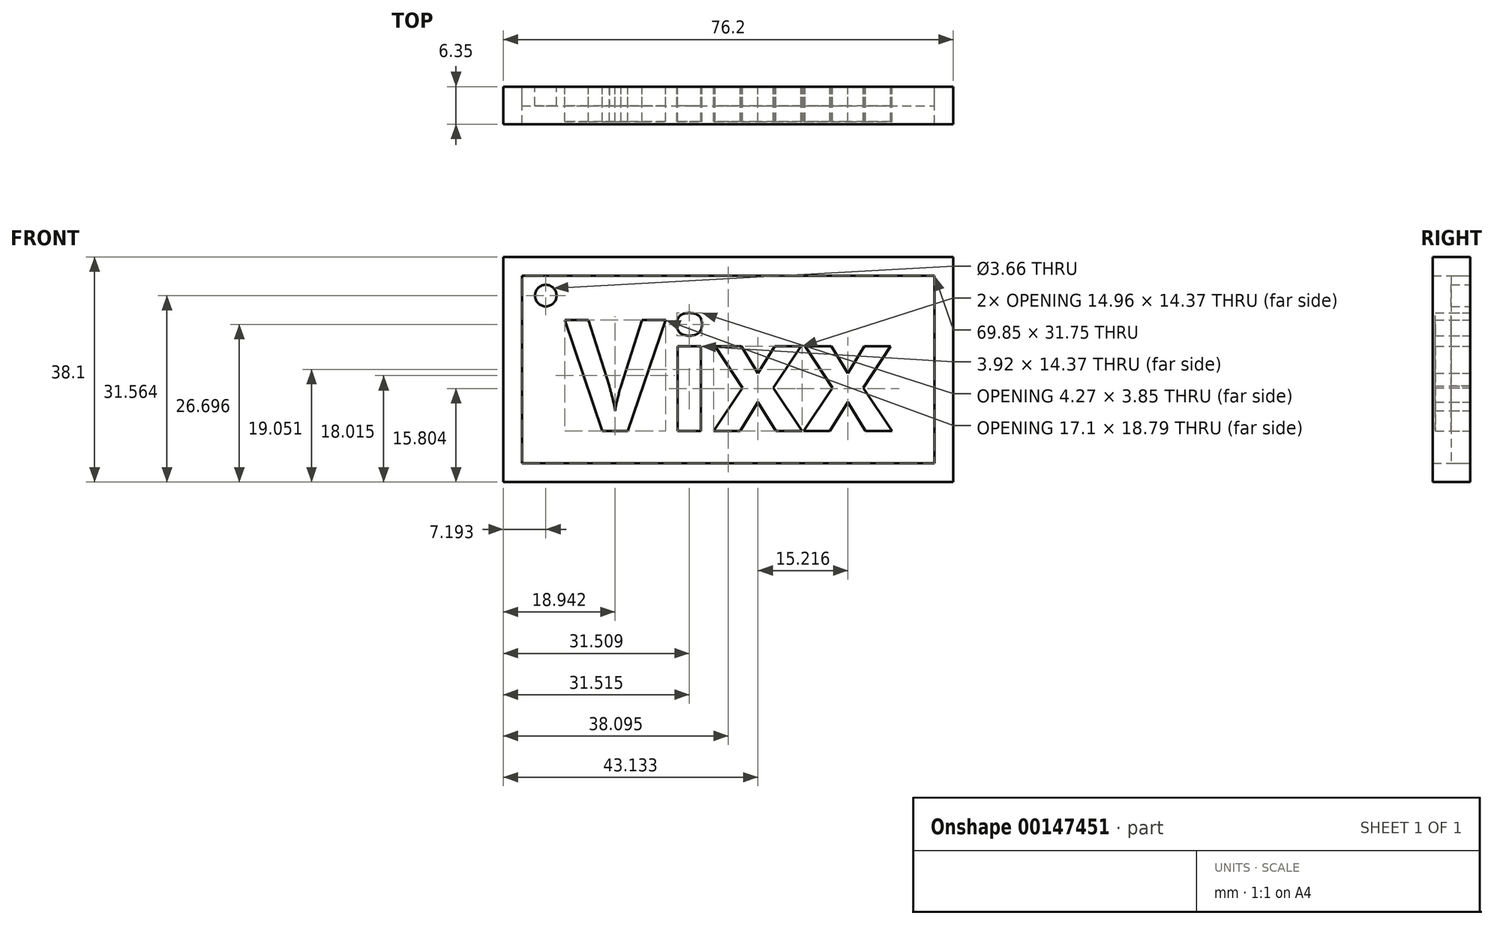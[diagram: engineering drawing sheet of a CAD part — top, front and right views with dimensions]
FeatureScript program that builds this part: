
annotation { "Feature Type Name" : "Feature", "Feature Type Description" : "" }
export const myFeature = defineFeature(function(context is Context, id is Id, definition is map)
    precondition{}
    {
        {
            var Q0;
            Q0=qCreatedBy(makeId("Front.planeOp"),FACE);
            var sketch = newSketch(context, id + "F0", { "sketchPlane" : qUnion([Q0])});
            skLineSegment(sketch, "E0.bottom", {"start": v(-39.35, 26.75) * mm, "end": v(36.85, 26.75) * mm});
            skLineSegment(sketch, "E0.top", {"start": v(-39.35, -11.35) * mm, "end": v(36.85, -11.35) * mm});
            skLineSegment(sketch, "E0.left", {"start": v(-39.35, 26.75) * mm, "end": v(-39.35, -11.35) * mm});
            skLineSegment(sketch, "E0.right", {"start": v(36.85, 26.75) * mm, "end": v(36.85, -11.35) * mm});
            skLineSegment(sketch, "E1.0", {"start": v(-36.18, 23.58) * mm, "end": v(33.67, 23.58) * mm});
            skLineSegment(sketch, "E1.1", {"start": v(-36.18, 23.58) * mm, "end": v(-36.18, -8.17) * mm});
            skLineSegment(sketch, "E1.2", {"start": v(-36.18, -8.17) * mm, "end": v(33.67, -8.17) * mm});
            skLineSegment(sketch, "E1.3", {"start": v(33.67, 23.58) * mm, "end": v(33.67, -8.17) * mm});
            skText(sketch, "E2", { "text": "Vixx", "fontName": "OpenSans-Bold.ttf"});
            skCircle(sketch, "E3", {"center": v(-32.16, 20.21) * mm, "radius": 1.83 * mm});
            const initialGuessF0  = {"E2": [-0.02896, -0.00273, 1, 0, 0.01895]};
            skSetInitialGuess(sketch, initialGuessF0);
            skSolve(sketch);
        }
        {
            var Q0;
            Q0=makeQuery(id+"F0.imprint","IMPRINT",FACE,{"disambiguationData":[TD([[makeQuery(id+"F0.imprint","IMPRINT",EDGE,{"derivedFrom":sQuery(id+"F0.wireOp",EDGE,"E2.sketch_text.stroke-0")}),-1.0]])]});
            var Q1;
            Q1=makeQuery(id+"F0.imprint","IMPRINT",FACE,{"disambiguationData":[TD([[makeQuery(id+"F0.imprint","IMPRINT",EDGE,{"derivedFrom":sQuery(id+"F0.wireOp",EDGE,"E2.sketch_text.stroke-15")}),-1.0]])]});
            var Q2;
            Q2=makeQuery(id+"F0.imprint","IMPRINT",FACE,{"disambiguationData":[TD([[makeQuery(id+"F0.imprint","IMPRINT",EDGE,{"derivedFrom":sQuery(id+"F0.wireOp",EDGE,"E2.sketch_text.stroke-10")}),-1.0]])]});
            var Q3;
            Q3=makeQuery(id+"F0.imprint","IMPRINT",FACE,{"disambiguationData":[TD([[makeQuery(id+"F0.imprint","IMPRINT",EDGE,{"derivedFrom":sQuery(id+"F0.wireOp",EDGE,"E2.sketch_text.stroke-19")}),-1.0]])]});
            var Q4;
            Q4=makeQuery(id+"F0.imprint","IMPRINT",FACE,{"disambiguationData":[TD([[makeQuery(id+"F0.imprint","IMPRINT",EDGE,{"derivedFrom":sQuery(id+"F0.wireOp",EDGE,"E2.sketch_text.stroke-31")}),-1.0]])]});
            extrude(context, id + "F1", {"entities" : qUnion([Q0, Q1, Q2, Q3, Q4]), "depth" : 5.9 * mm});
        }
        {
            var Q0;
            Q0=makeQuery(id+"F0.imprint","IMPRINT",FACE,{"disambiguationData":[TD([[makeQuery(id+"F0.imprint","IMPRINT",EDGE,{"derivedFrom":sQuery(id+"F0.wireOp",EDGE,"E0.bottom")}),-1.0]])]});
            extrude(context, id + "F2", {"entities" : qUnion([Q0]), "depth" : 6.35 * mm});
        }
        {
            var Q0;
            Q0=makeQuery(id+"F0.imprint","IMPRINT",FACE,{"disambiguationData":[TD([[makeQuery(id+"F0.imprint","IMPRINT",EDGE,{"derivedFrom":sQuery(id+"F0.wireOp",EDGE,"E1.0")}),-1.0]])]});
            extrude(context, id + "F3", {"entities" : qUnion([Q0]), "depth" : 3.24 * mm});
        }
    });
